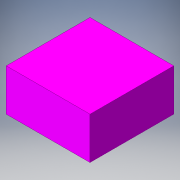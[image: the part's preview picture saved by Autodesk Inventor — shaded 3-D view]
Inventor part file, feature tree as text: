
AUTODESK INVENTOR PART (.ipt)
format: ipt  version: 2016 (Build 200138000, 138)  size: 96,256 bytes
history: native  units: in
note: dims shown in document units (in); Inventor stores cm internally (conversion verified against a paired STEP export)
features: extrude x1, sketch x1
ambient origin geometry x8: Origin, YZ Plane, XZ Plane, XY Plane, X Axis, Y Axis, Z Axis, Center Point
bodies: Solid1 (feature_tree)
feature tree (2):
  extrude  "Extrusion1"  Depth=1.0in
  sketch  "Sketch1"  dims[d0=2.0in d1=1.0in d2=2.0in d3=0.0in]
